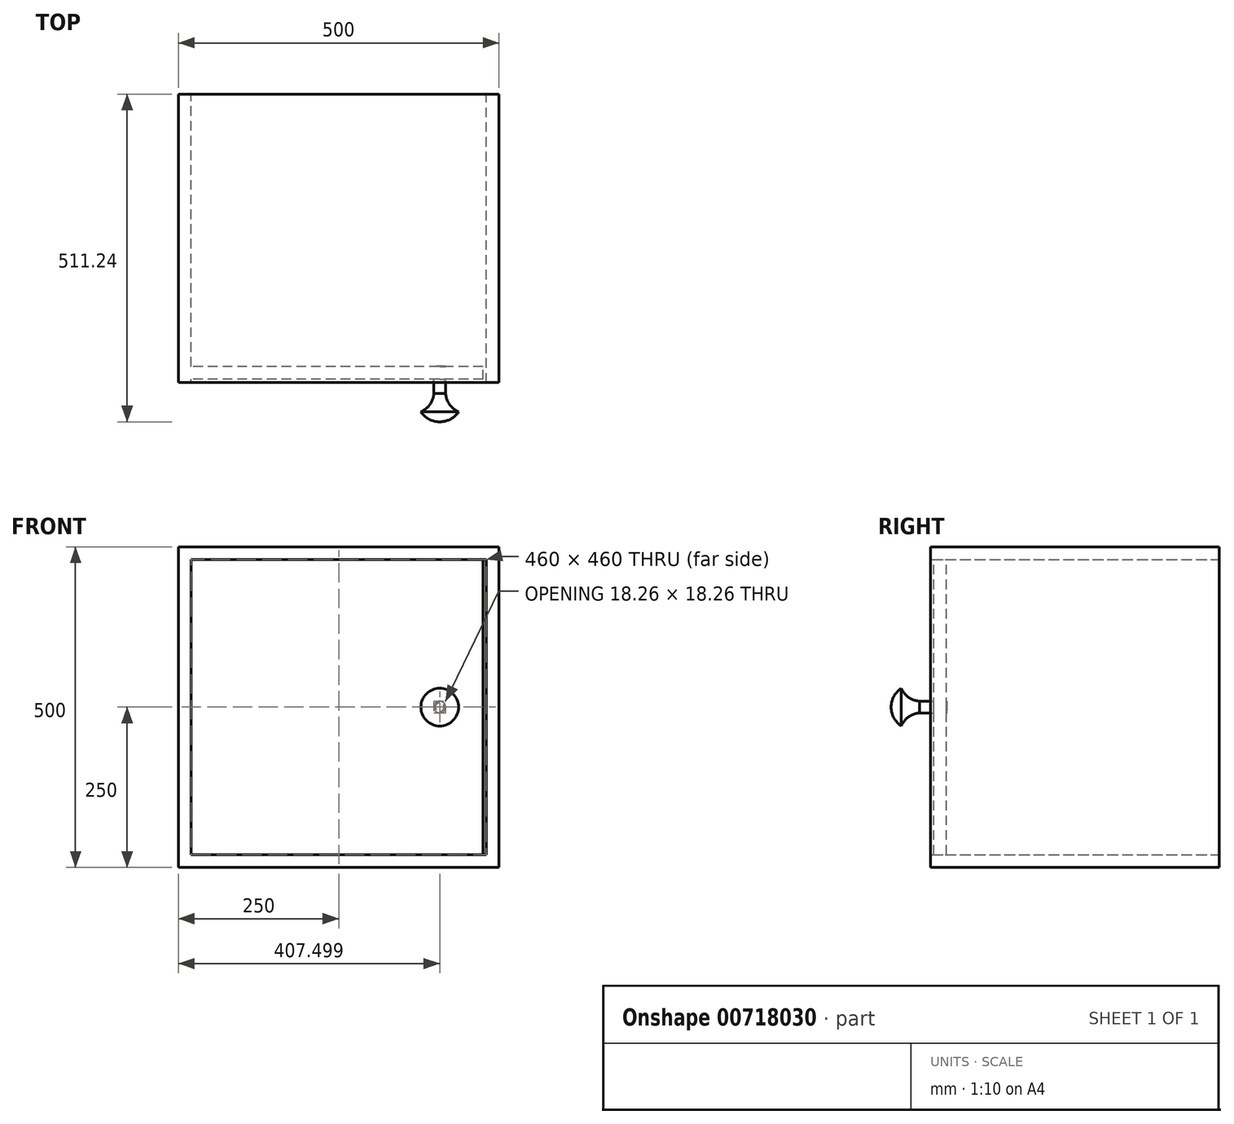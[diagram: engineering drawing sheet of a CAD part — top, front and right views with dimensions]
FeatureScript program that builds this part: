
annotation { "Feature Type Name" : "Feature", "Feature Type Description" : "" }
export const myFeature = defineFeature(function(context is Context, id is Id, definition is map)
    precondition{}
    {
        {
            var Q0;
            Q0=qCreatedBy(makeId("Front.planeOp"),FACE);
            var sketch = newSketch(context, id + "F0", { "sketchPlane" : qUnion([Q0])});
            skLineSegment(sketch, "E0.bottom", {"start": v(250, 250) * mm, "end": v(-250, 250) * mm});
            skLineSegment(sketch, "E0.top", {"start": v(250, -250) * mm, "end": v(-250, -250) * mm});
            skLineSegment(sketch, "E0.left", {"start": v(250, 250) * mm, "end": v(250, -250) * mm});
            skLineSegment(sketch, "E0.right", {"start": v(-250, 250) * mm, "end": v(-250, -250) * mm});
            skPoint(sketch, "E0.middle", {"position": v(0, 0) * mm});
            skLineSegment(sketch, "E1.0", {"start": v(-230, 230) * mm, "end": v(-230, -230) * mm});
            skLineSegment(sketch, "E1.1", {"start": v(230, 230) * mm, "end": v(-230, 230) * mm});
            skLineSegment(sketch, "E1.2", {"start": v(230, 230) * mm, "end": v(230, -230) * mm});
            skLineSegment(sketch, "E1.3", {"start": v(230, -230) * mm, "end": v(-230, -230) * mm});
            skSolve(sketch);
        }
        {
            var Q0;
            Q0 = qSketchRegion(id + "F0", true);
            extrude(context, id + "F1", {"entities" : qUnion([Q0]), "depth" : 450 * mm, "offsetDistance" : 25 * mm});
        }
        {
            var Q0;
            Q0=makeQuery(id+"F1.opExtrude","SWEPT_FACE",FACE,{"disambiguationData":[OSD([sQuery(id+"F0.wireOp",EDGE,"E1.0")])]});
            var sketch = newSketch(context, id + "F2", { "sketchPlane" : qUnion([Q0])});
            skLineSegment(sketch, "E2.bottom", {"start": v(-445, -230) * mm, "end": v(-425, -230) * mm});
            skLineSegment(sketch, "E2.top", {"start": v(-445, 230) * mm, "end": v(-425, 230) * mm});
            skLineSegment(sketch, "E2.left", {"start": v(-445, -230) * mm, "end": v(-445, 230) * mm});
            skLineSegment(sketch, "E2.right", {"start": v(-425, -230) * mm, "end": v(-425, 230) * mm});
            skSolve(sketch);
        }
        {
            var Q0;
            Q0 = qSketchRegion(id + "F2", true);
            extrude(context, id + "F3", {"entities" : qUnion([Q0]), "operationType" : NewBodyOperationType.ADD, "depth" : 455 * mm, "offsetDistance" : 25 * mm});
        }
        {
            var Q0;
            Q0=qCreatedBy(makeId("Top.planeOp"),FACE);
            var sketch = newSketch(context, id + "F4", { "sketchPlane" : qUnion([Q0])});
            skLineSegment(sketch, "E3", {"start": v(157.5, -426.54) * mm, "end": v(157.5, -511.24) * mm});
            skArc(sketch, "E4", {"start": v(157.5, -511.24) * mm, "mid": v(174.17, -507.08) * mm, "end": v(186.92, -495.58) * mm});
            skArc(sketch, "E5", {"start": v(186.92, -495.58) * mm, "mid": v(172.75, -483.99) * mm, "end": v(166.63, -466.73) * mm});
            skLineSegment(sketch, "E6", {"start": v(166.63, -466.73) * mm, "end": v(166.63, -424.46) * mm});
            skLineSegment(sketch, "E7", {"start": v(166.63, -424.46) * mm, "end": v(157.5, -426.54) * mm});
            skSolve(sketch);
        }
        {
            var Q0;
            Q0=makeQuery(id+"F4.imprint","IMPRINT",FACE,{"disambiguationData":[TD([[makeQuery(id+"F4.imprint","IMPRINT",EDGE,{"derivedFrom":sQuery(id+"F4.wireOp",EDGE,"E3")}),1.0]])]});
            var Q1;
            Q1=sQuery(id+"F4.wireOp",EDGE,"E3");
            revolve(context, id + "F5", {"operationType" : NewBodyOperationType.ADD, "surfaceOperationType" : NewSurfaceOperationType.NEW, "entities" : qUnion([Q0]), "axis" : qUnion([Q1]), "revolveType" : RevolveType.FULL});
        }
    });
